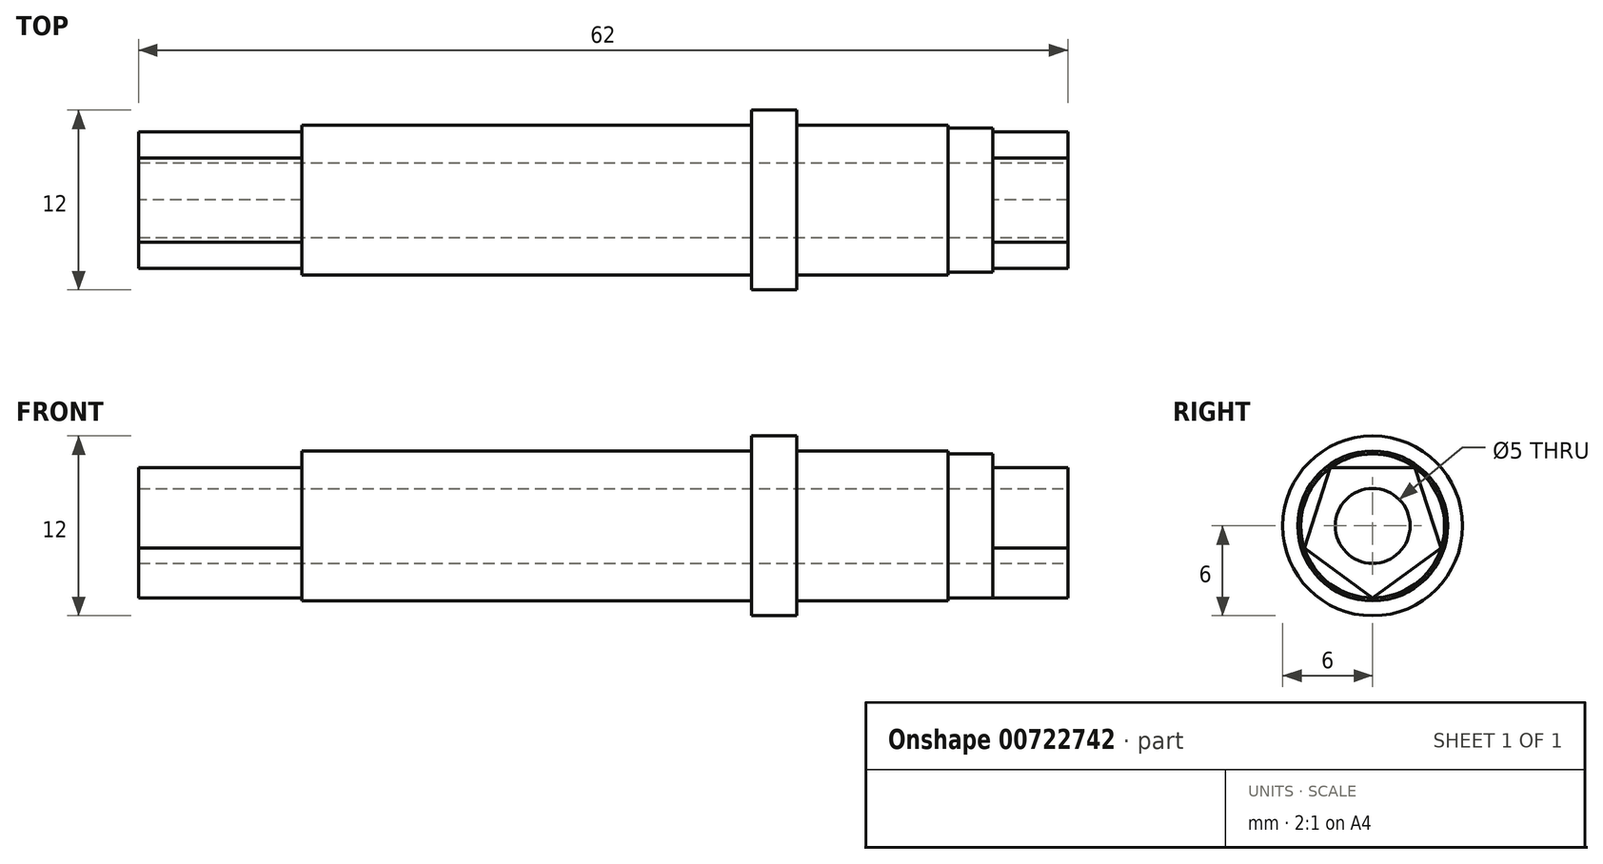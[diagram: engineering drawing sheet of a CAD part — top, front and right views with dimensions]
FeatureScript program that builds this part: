
annotation { "Feature Type Name" : "Feature", "Feature Type Description" : "" }
export const myFeature = defineFeature(function(context is Context, id is Id, definition is map)
    precondition{}
    {
        {
            var Q0;
            Q0=qCreatedBy(makeId("Right.planeOp"),FACE);
            var sketch = newSketch(context, id + "F0", { "sketchPlane" : qUnion([Q0])});
            skCircle(sketch, "E0", {"center": v(0, 0) * mm, "radius": 5 * mm});
            skSolve(sketch);
        }
        {
            var Q0;
            Q0=qSketchRegion(id+"F0",true);
            extrude(context, id + "F1", {"entities" : qUnion([Q0]), "oppositeDirection" : true, "depth" : 10.1 * mm, "offsetDistance" : 25 * mm});
        }
        {
            var Q0;
            Q0=makeQuery(id+"F1.opExtrude","CAP_FACE",FACE,{"disambiguationData":[OSD([sQuery(id+"F0.wireOp",EDGE,"E0")])],"isStart":true});
            var sketch = newSketch(context, id + "F2", { "sketchPlane" : qUnion([Q0])});
            skCircle(sketch, "E1", {"center": v(0, 0) * mm, "radius": 4.8 * mm});
            skSolve(sketch);
        }
        {
            var Q0;
            Q0=qSketchRegion(id+"F2",true);
            extrude(context, id + "F3", {"entities" : qUnion([Q0]), "operationType" : NewBodyOperationType.ADD, "depth" : 3 * mm, "offsetDistance" : 25 * mm});
        }
        {
            var Q0;
            Q0=makeQuery(id+"F3.opExtrude","CAP_FACE",FACE,{"disambiguationData":[OSD([sQuery(id+"F2.wireOp",EDGE,"E1")])],"isStart":false});
            var sketch = newSketch(context, id + "F4", { "sketchPlane" : qUnion([Q0])});
            skCircle(sketch, "E2.cCircle", {"center": v(0, 0) * mm, "radius": 4.8 * mm, "construction": true});
            skLineSegment(sketch, "E2.0", {"start": v(0, -4.8) * mm, "end": v(-4.57, -1.48) * mm});
            skLineSegment(sketch, "E2.1", {"start": v(-4.57, -1.48) * mm, "end": v(-2.82, 3.88) * mm});
            skLineSegment(sketch, "E2.2", {"start": v(-2.82, 3.88) * mm, "end": v(2.82, 3.88) * mm});
            skLineSegment(sketch, "E2.3", {"start": v(2.82, 3.88) * mm, "end": v(4.57, -1.48) * mm});
            skLineSegment(sketch, "E2.4", {"start": v(4.57, -1.48) * mm, "end": v(0, -4.8) * mm});
            skSolve(sketch);
        }
        {
            var Q0;
            Q0=qSketchRegion(id+"F4",true);
            extrude(context, id + "F5", {"entities" : qUnion([Q0]), "operationType" : NewBodyOperationType.ADD, "depth" : 5 * mm, "offsetDistance" : 25 * mm, "hasSecondDirection" : true, "secondDirectionOppositeDirection" : true, "secondDirectionDepth" : 57 * mm});
        }
        {
            var Q0;
            Q0=makeQuery(id+"F1.opExtrude","CAP_FACE",FACE,{"disambiguationData":[OSD([sQuery(id+"F0.wireOp",EDGE,"E0")])],"isStart":false});
            var sketch = newSketch(context, id + "F6", { "sketchPlane" : qUnion([Q0])});
            skCircle(sketch, "E3", {"center": v(0, 0) * mm, "radius": 6 * mm});
            skSolve(sketch);
        }
        {
            var Q0;
            Q0=qSketchRegion(id+"F6",true);
            extrude(context, id + "F7", {"entities" : qUnion([Q0]), "operationType" : NewBodyOperationType.ADD, "depth" : 3 * mm, "offsetDistance" : 25 * mm});
        }
        {
            var Q0;
            {var subQ0=sQuery(id+"F6.wireOp",EDGE,"E3");Q0=makeQuery(id+"F7.boolean.opBoolean","SPLIT",FACE,{"disambiguationData":[TD([makeQuery(id+"F5.opExtrude","SWEPT_FACE",FACE,{"disambiguationData":[OSD([sQuery(id+"F4.wireOp",EDGE,"E2.0")])]})])],"derivedFrom":makeQuery(id+"F7.opExtrude","CAP_FACE",FACE,{"disambiguationData":[OSD([subQ0])],"isStart":false})});}
            var sketch = newSketch(context, id + "F8", { "sketchPlane" : qUnion([Q0])});
            skCircle(sketch, "E4", {"center": v(0, 0) * mm, "radius": 5 * mm});
            skSolve(sketch);
        }
        {
            var Q0;
            Q0=qSketchRegion(id+"F8",true);
            extrude(context, id + "F9", {"entities" : qUnion([Q0]), "operationType" : NewBodyOperationType.ADD, "depth" : 30 * mm, "offsetDistance" : 25 * mm});
        }
        {
            var Q0;
            Q0=makeQuery(id+"F5.opExtrude","CAP_FACE",FACE,{"disambiguationData":[OSD([sQuery(id+"F4.wireOp",EDGE,"E2.0"),sQuery(id+"F4.wireOp",EDGE,"E2.1"),sQuery(id+"F4.wireOp",EDGE,"E2.2"),sQuery(id+"F4.wireOp",EDGE,"E2.3"),sQuery(id+"F4.wireOp",EDGE,"E2.4")])],"isStart":false});
            var sketch = newSketch(context, id + "F10", { "sketchPlane" : qUnion([Q0])});
            skCircle(sketch, "E5", {"center": v(0, 0) * mm, "radius": 2.5 * mm});
            skSolve(sketch);
        }
        {
            var Q0;
            Q0=qSketchRegion(id+"F10",true);
            extrude(context, id + "F11", {"entities" : qUnion([Q0]), "operationType" : NewBodyOperationType.REMOVE, "oppositeDirection" : true, "depth" : 80 * mm, "offsetDistance" : 25 * mm});
        }
    });
